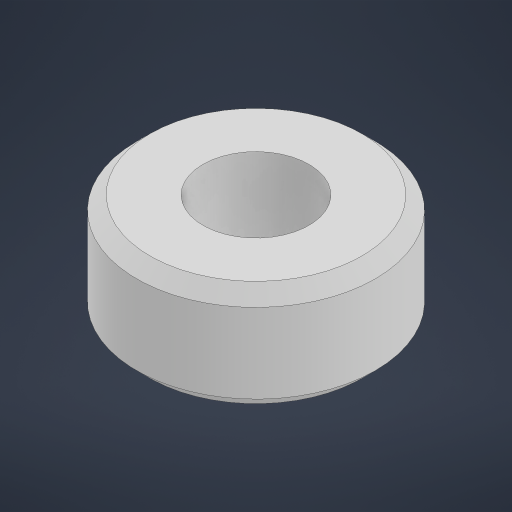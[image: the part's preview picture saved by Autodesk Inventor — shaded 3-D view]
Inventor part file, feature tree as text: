
AUTODESK INVENTOR PART (.ipt)
format: ipt  version: 2024 (Build 280153000, 153)  size: 168,960 bytes
history: native  units: in
note: dims shown in document units (in); Inventor stores cm internally (conversion verified against a paired STEP export)
features: extrude x1, chamfer x1, sketch x1
ambient origin geometry x8: Origin, YZ Plane, XZ Plane, XY Plane, X Axis, Y Axis, Z Axis, Center Point
bodies: Solid1 (feature_tree)
feature tree (3):
  extrude  "Extrusion1"  Depth=0.0787in
  chamfer  "Chamfer1"  Distance=0.1575in
  sketch  "Sketch1"  dims[d0=0.1575in d1=0.3543in d2=0.1575in d3=0.0in d4=0.0197in d5=0.0787in d6=45.0deg]
